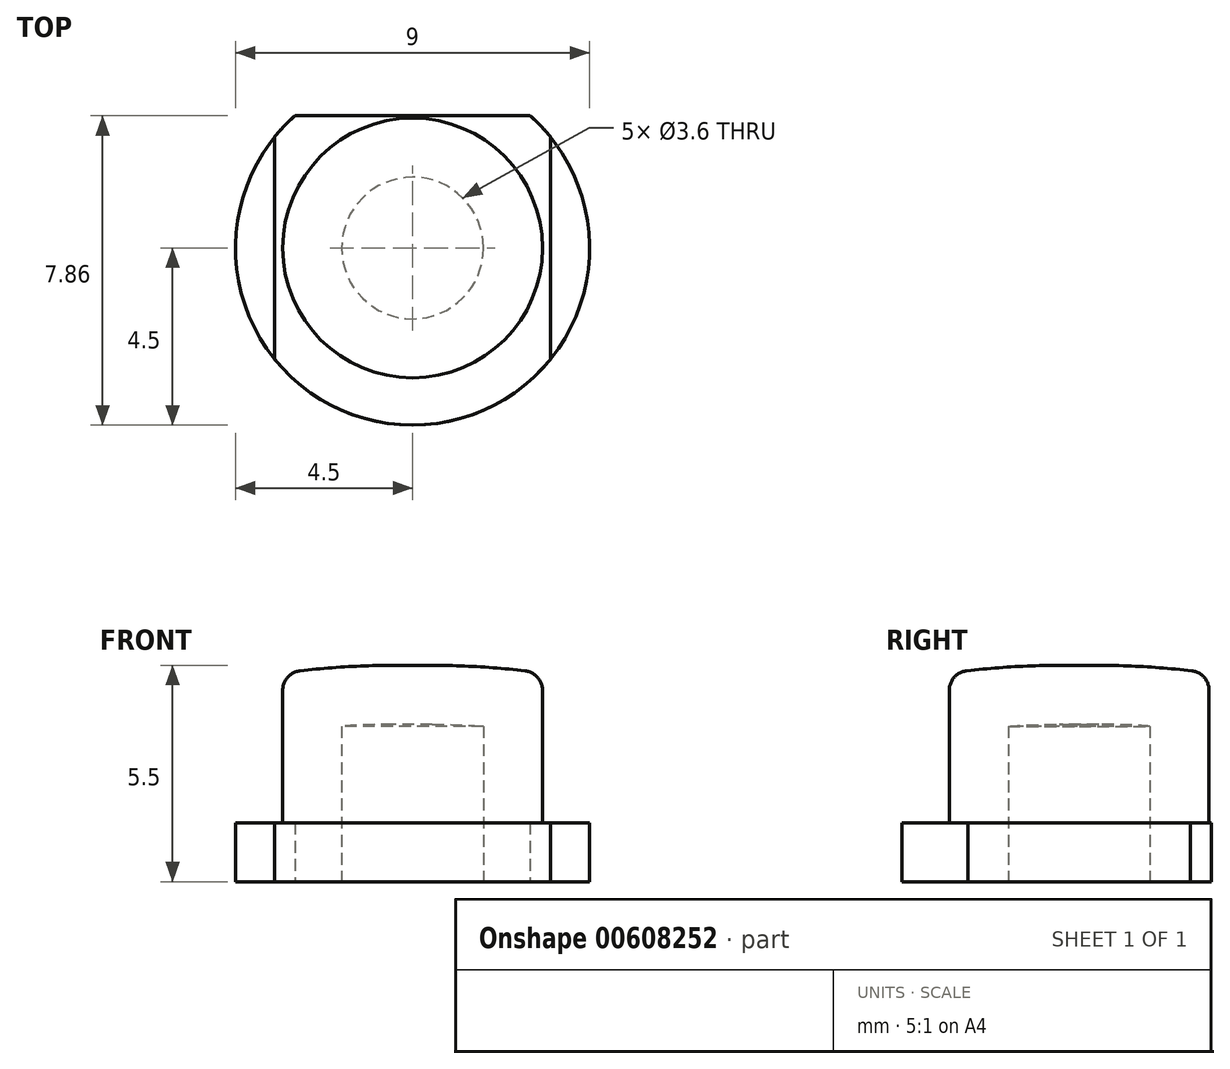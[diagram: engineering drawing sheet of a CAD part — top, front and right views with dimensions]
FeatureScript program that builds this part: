
annotation { "Feature Type Name" : "Feature", "Feature Type Description" : "" }
export const myFeature = defineFeature(function(context is Context, id is Id, definition is map)
    precondition{}
    {
        {
            var Q0;
            Q0=qCreatedBy(makeId("Front.planeOp"),FACE);
            var sketch = newSketch(context, id + "F0", { "sketchPlane" : qUnion([Q0])});
            skLineSegment(sketch, "E0", {"start": v(0, -1.55) * mm, "end": v(0, 3.95) * mm});
            skLineSegment(sketch, "E1", {"start": v(3.3, 3.75) * mm, "end": v(3.3, -0.05) * mm});
            skLineSegment(sketch, "E2", {"start": v(3.3, -0.05) * mm, "end": v(4.5, -0.05) * mm});
            skLineSegment(sketch, "E3", {"start": v(4.5, -0.05) * mm, "end": v(4.5, -1.55) * mm});
            skLineSegment(sketch, "E4", {"start": v(4.5, -1.55) * mm, "end": v(0, -1.55) * mm});
            skLineSegment(sketch, "E5", {"start": v(0, 3.95) * mm, "end": v(0.5, 3.95) * mm});
            skArc(sketch, "E6", {"start": v(3.3, 3.75) * mm, "mid": v(1.9, 3.9) * mm, "end": v(0.5, 3.95) * mm});
            skSolve(sketch);
        }
        {
            var Q0;
            Q0=qSketchRegion(id+"F0",true);
            var Q1;
            Q1=sQuery(id+"F0.wireOp",EDGE,"E0");
            revolve(context, id + "F1", {"entities" : qUnion([Q0]), "axis" : qUnion([Q1]), "revolveType" : RevolveType.FULL});
        }
        {
            var Q0;
            Q0=makeQuery(id+"F1.opRevolve","SWEPT_EDGE",EDGE,{"disambiguationData":[OSD([sQuery(id+"F0.wireOp",EDGE,"E1"),sQuery(id+"F0.wireOp",EDGE,"E6")])]});
            fillet(context, id + "F2", {"entities" : qUnion([Q0]), "radius" : 0.5 * mm, "tangentPropagation" : true, "allowEdgeOverflow" : false});
        }
        {
            var Q0;
            Q0=makeQuery(id+"F1.opRevolve","SWEPT_FACE",FACE,{"disambiguationData":[OSD([sQuery(id+"F0.wireOp",EDGE,"E4")])]});
            shell(context, id + "F3", {"entities" : qUnion([Q0]), "thickness" : 1.5 * mm});
        }
        {
            var Q0;
            Q0=makeQuery(id+"F1.opRevolve","SWEPT_BODY",BODY,{"disambiguationData":[OSD([sQuery(id+"F0.wireOp",EDGE,"E0"),sQuery(id+"F0.wireOp",EDGE,"E1"),sQuery(id+"F0.wireOp",EDGE,"E2"),sQuery(id+"F0.wireOp",EDGE,"E3"),sQuery(id+"F0.wireOp",EDGE,"E4"),sQuery(id+"F0.wireOp",EDGE,"E5"),sQuery(id+"F0.wireOp",EDGE,"E6")])]});
            transform(context, id + "F4", {"entities" : qUnion([Q0]), "transformType" : TransformType.COPY});
        }
        {
            var Q0;
            Q0=qCreatedBy(makeId("Top.planeOp"),FACE);
            var sketch = newSketch(context, id + "F5", { "sketchPlane" : qUnion([Q0])});
            skLineSegment(sketch, "E7.bottom", {"start": v(3.5, 7.34) * mm, "end": v(6.77, 7.34) * mm});
            skLineSegment(sketch, "E7.top", {"start": v(3.5, -6.74) * mm, "end": v(6.77, -6.74) * mm});
            skLineSegment(sketch, "E7.left", {"start": v(3.5, 7.34) * mm, "end": v(3.5, -6.74) * mm});
            skLineSegment(sketch, "E7.right", {"start": v(6.77, 7.34) * mm, "end": v(6.77, -6.74) * mm});
            skSolve(sketch);
        }
        {
            var Q0;
            Q0=qSketchRegion(id+"F5",true);
            extrude(context, id + "F6", {"entities" : qUnion([Q0]), "operationType" : NewBodyOperationType.REMOVE, "oppositeDirection" : true, "depth" : 25 * mm, "offsetDistance" : 25 * mm});
        }
        {
            var Q0;
            Q0=makeQuery(id+"F4.opPattern","COPY",BODY,{"derivedFrom":makeQuery(id+"F1.opRevolve","SWEPT_BODY",BODY,{"disambiguationData":[OSD([sQuery(id+"F0.wireOp",EDGE,"E0"),sQuery(id+"F0.wireOp",EDGE,"E1"),sQuery(id+"F0.wireOp",EDGE,"E2"),sQuery(id+"F0.wireOp",EDGE,"E3"),sQuery(id+"F0.wireOp",EDGE,"E4"),sQuery(id+"F0.wireOp",EDGE,"E5"),sQuery(id+"F0.wireOp",EDGE,"E6")])]}),"instanceName":"1"});
            var Q1;
            Q1=qCreatedBy(makeId("Right.planeOp"),FACE);
            mirror(context, id + "F7", {"entities" : qUnion([Q0]), "mirrorPlane" : qUnion([Q1])});
        }
        {
            var Q0;
            Q0=makeQuery(id+"F4.opPattern","COPY",BODY,{"derivedFrom":makeQuery(id+"F1.opRevolve","SWEPT_BODY",BODY,{"disambiguationData":[OSD([sQuery(id+"F0.wireOp",EDGE,"E0"),sQuery(id+"F0.wireOp",EDGE,"E1"),sQuery(id+"F0.wireOp",EDGE,"E2"),sQuery(id+"F0.wireOp",EDGE,"E3"),sQuery(id+"F0.wireOp",EDGE,"E4"),sQuery(id+"F0.wireOp",EDGE,"E5"),sQuery(id+"F0.wireOp",EDGE,"E6")])]}),"instanceName":"1"});
            var Q1;
            Q1=makeQuery(id+"F7.opPattern","COPY",BODY,{"derivedFrom":makeQuery(id+"F4.opPattern","COPY",BODY,{"derivedFrom":makeQuery(id+"F1.opRevolve","SWEPT_BODY",BODY,{"disambiguationData":[OSD([sQuery(id+"F0.wireOp",EDGE,"E0"),sQuery(id+"F0.wireOp",EDGE,"E1"),sQuery(id+"F0.wireOp",EDGE,"E2"),sQuery(id+"F0.wireOp",EDGE,"E3"),sQuery(id+"F0.wireOp",EDGE,"E4"),sQuery(id+"F0.wireOp",EDGE,"E5"),sQuery(id+"F0.wireOp",EDGE,"E6")])]}),"instanceName":"1"}),"instanceName":"1"});
            transform(context, id + "F8", {"entities" : qUnion([Q0, Q1]), "transformType" : TransformType.COPY});
        }
        {
            var Q0;
            Q0=qCreatedBy(makeId("Top.planeOp"),FACE);
            var sketch = newSketch(context, id + "F9", { "sketchPlane" : qUnion([Q0])});
            skLineSegment(sketch, "E8.bottom", {"start": v(-6.07, 5.42) * mm, "end": v(5.37, 5.42) * mm});
            skLineSegment(sketch, "E8.top", {"start": v(-6.07, 3.36) * mm, "end": v(5.37, 3.36) * mm});
            skLineSegment(sketch, "E8.left", {"start": v(-6.07, 5.42) * mm, "end": v(-6.07, 3.36) * mm});
            skLineSegment(sketch, "E8.right", {"start": v(5.37, 5.42) * mm, "end": v(5.37, 3.36) * mm});
            skSolve(sketch);
        }
        {
            var Q0;
            Q0 = qSketchRegion(id + "F9", true);
            extrude(context, id + "F10", {"entities" : qUnion([Q0]), "operationType" : NewBodyOperationType.REMOVE, "oppositeDirection" : true, "depth" : 25 * mm, "offsetDistance" : 25 * mm});
        }
    });
